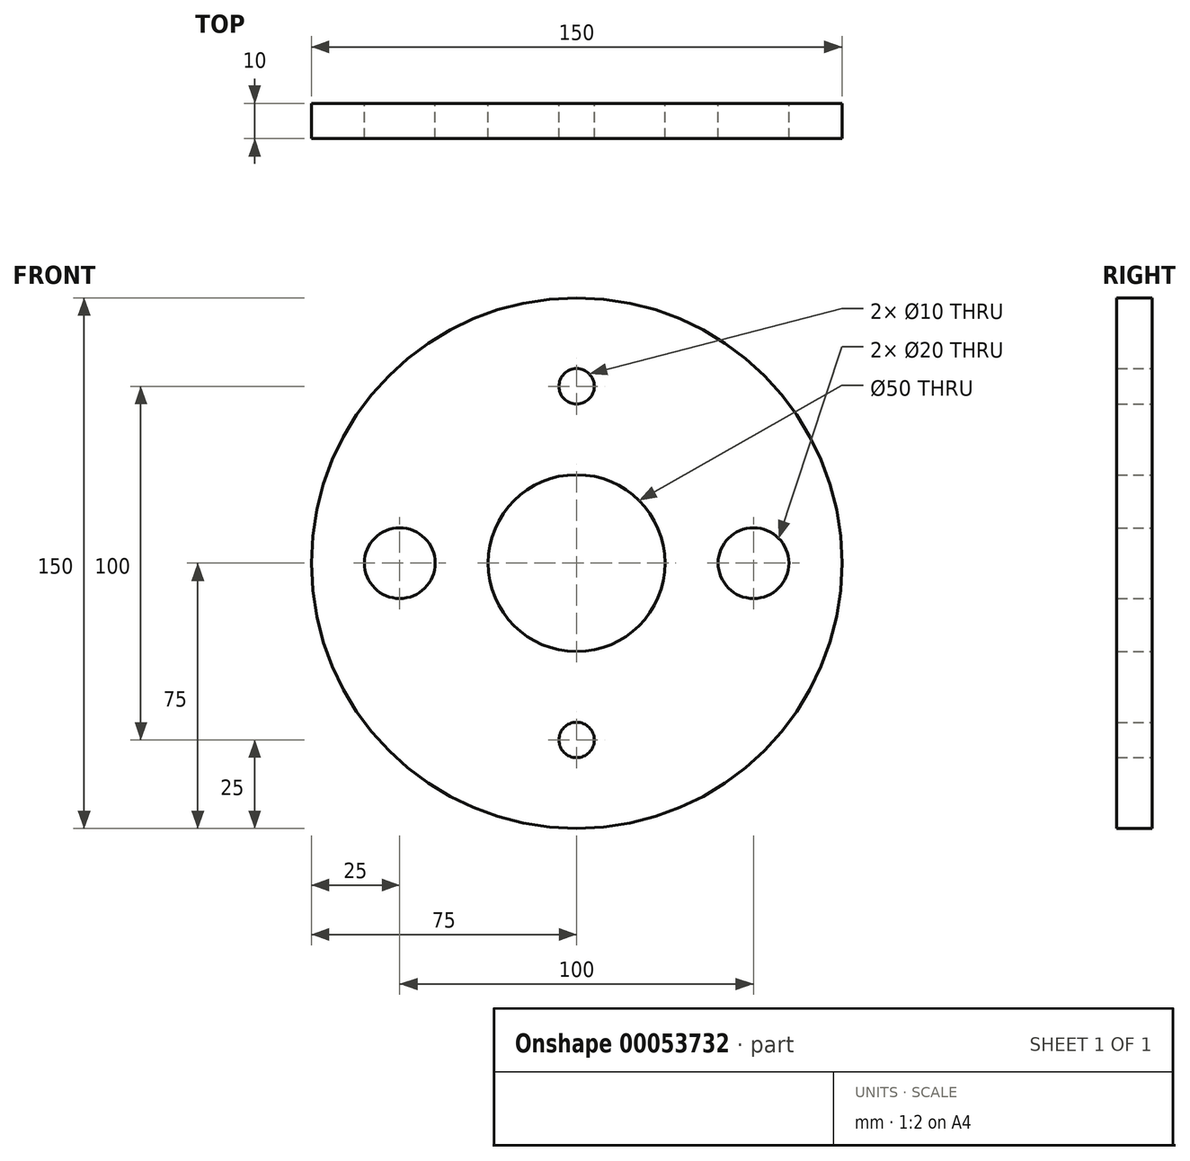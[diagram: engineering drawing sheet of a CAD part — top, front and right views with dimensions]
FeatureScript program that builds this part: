
annotation { "Feature Type Name" : "Feature", "Feature Type Description" : "" }
export const myFeature = defineFeature(function(context is Context, id is Id, definition is map)
    precondition{}
    {
        {
            var Q0;
            Q0=qCreatedBy(makeId("Front.planeOp"),FACE);
            var sketch = newSketch(context, id + "F0", { "sketchPlane" : qUnion([Q0])});
            skCircle(sketch, "E0", {"center": v(0, 0) * mm, "radius": 75 * mm});
            skCircle(sketch, "E1", {"center": v(0, 50) * mm, "radius": 5 * mm});
            skCircle(sketch, "E2", {"center": v(0, -50) * mm, "radius": 5 * mm});
            skCircle(sketch, "E3", {"center": v(50, 0) * mm, "radius": 10 * mm});
            skCircle(sketch, "E4", {"center": v(-50, 0) * mm, "radius": 10 * mm});
            skCircle(sketch, "E5", {"center": v(0, 0) * mm, "radius": 25 * mm});
            skSolve(sketch);
        }
        {
            var Q0;
            Q0=makeQuery(id+"F0.imprint","IMPRINT",FACE,{"disambiguationData":[TD([[makeQuery(id+"F0.imprint","IMPRINT",EDGE,{"derivedFrom":sQuery(id+"F0.wireOp",EDGE,"E0")}),1.0]])]});
            extrude(context, id + "F1", {"entities" : qUnion([Q0]), "depth" : 10 * mm});
        }
    });
